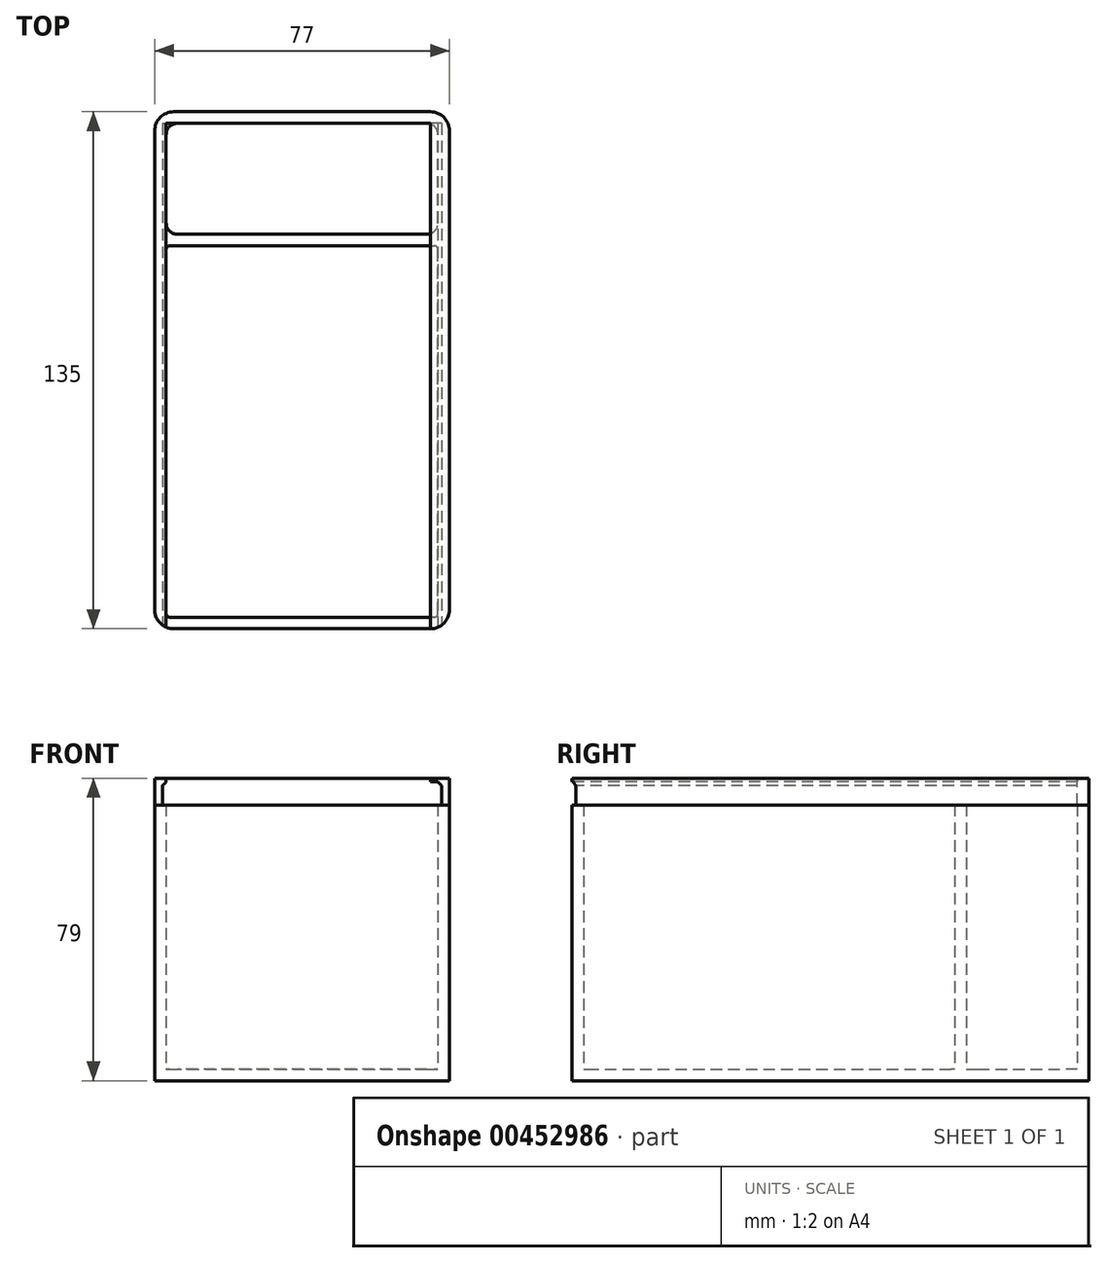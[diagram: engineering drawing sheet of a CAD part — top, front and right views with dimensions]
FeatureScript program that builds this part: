
annotation { "Feature Type Name" : "Feature", "Feature Type Description" : "" }
export const myFeature = defineFeature(function(context is Context, id is Id, definition is map)
    precondition{}
    {
        {
            var Q0;
            Q0=qCreatedBy(makeId("Top.planeOp"),FACE);
            var sketch = newSketch(context, id + "F0", { "sketchPlane" : qUnion([Q0])});
            skLineSegment(sketch, "E0.bottom", {"start": v(42.74, -68.6) * mm, "end": v(-26.26, -68.6) * mm});
            skLineSegment(sketch, "E0.top", {"start": v(43.74, 31.4) * mm, "end": v(-27.26, 31.4) * mm});
            skLineSegment(sketch, "E0.left", {"start": v(43.74, -67.6) * mm, "end": v(43.74, 27.4) * mm});
            skLineSegment(sketch, "E0.right", {"start": v(-27.26, -67.6) * mm, "end": v(-27.26, 27.4) * mm});
            skLineSegment(sketch, "E1.bottom", {"start": v(-27.26, 31.4) * mm, "end": v(43.74, 31.4) * mm});
            skLineSegment(sketch, "E1.top", {"start": v(-24.26, 60.4) * mm, "end": v(40.74, 60.4) * mm});
            skLineSegment(sketch, "E1.left", {"start": v(-27.26, 34.4) * mm, "end": v(-27.26, 57.4) * mm});
            skLineSegment(sketch, "E1.right", {"start": v(43.74, 34.4) * mm, "end": v(43.74, 57.4) * mm});
            skLineSegment(sketch, "E2.bottom", {"start": v(-26.26, 31.4) * mm, "end": v(42.74, 31.4) * mm});
            skLineSegment(sketch, "E2.top", {"start": v(-26.26, 28.4) * mm, "end": v(42.74, 28.4) * mm});
            skLineSegment(sketch, "E2.left", {"start": v(-27.26, 30.4) * mm, "end": v(-27.26, 29.4) * mm});
            skLineSegment(sketch, "E2.right", {"start": v(43.74, 30.4) * mm, "end": v(43.74, 29.4) * mm});
            skLineSegment(sketch, "E3.bottom", {"start": v(-25.26, 63.4) * mm, "end": v(41.74, 63.4) * mm});
            skLineSegment(sketch, "E3.top", {"start": v(-25.26, -71.6) * mm, "end": v(41.74, -71.6) * mm});
            skLineSegment(sketch, "E3.left", {"start": v(-30.26, 58.4) * mm, "end": v(-30.26, -66.6) * mm});
            skLineSegment(sketch, "E3.right", {"start": v(46.74, 58.4) * mm, "end": v(46.74, -66.6) * mm});
            skPoint(sketch, "E4.visualSharp", {"position": v(-30.26, 63.4) * mm});
            skArc(sketch, "E4.filletArc", {"start": v(-25.26, 63.4) * mm, "mid": v(-28.8, 61.94) * mm, "end": v(-30.26, 58.4) * mm});
            skPoint(sketch, "E5.visualSharp", {"position": v(46.74, 63.4) * mm});
            skArc(sketch, "E5.filletArc", {"start": v(46.74, 58.4) * mm, "mid": v(45.28, 61.94) * mm, "end": v(41.74, 63.4) * mm});
            skPoint(sketch, "E6.visualSharp", {"position": v(46.74, -71.6) * mm});
            skArc(sketch, "E6.filletArc", {"start": v(41.74, -71.6) * mm, "mid": v(45.28, -70.13) * mm, "end": v(46.74, -66.6) * mm});
            skPoint(sketch, "E7.visualSharp", {"position": v(-30.26, -71.6) * mm});
            skArc(sketch, "E7.filletArc", {"start": v(-30.26, -66.6) * mm, "mid": v(-28.8, -70.13) * mm, "end": v(-25.26, -71.6) * mm});
            skPoint(sketch, "E8.visualSharp", {"position": v(-27.26, -68.6) * mm});
            skArc(sketch, "E8.filletArc", {"start": v(-27.26, -67.6) * mm, "mid": v(-26.97, -68.3) * mm, "end": v(-26.26, -68.6) * mm});
            skPoint(sketch, "E9.visualSharp", {"position": v(43.74, -68.6) * mm});
            skArc(sketch, "E9.filletArc", {"start": v(42.74, -68.6) * mm, "mid": v(43.45, -68.3) * mm, "end": v(43.74, -67.6) * mm});
            skArc(sketch, "E10.filletArc", {"start": v(-26.26, 28.4) * mm, "mid": v(-26.97, 28.11) * mm, "end": v(-27.26, 27.4) * mm});
            skArc(sketch, "E11.filletArc", {"start": v(-27.26, 29.4) * mm, "mid": v(-26.97, 28.7) * mm, "end": v(-26.26, 28.4) * mm});
            skArc(sketch, "E12.filletArc", {"start": v(43.74, 27.4) * mm, "mid": v(43.45, 28.11) * mm, "end": v(42.74, 28.4) * mm});
            skArc(sketch, "E13.filletArc", {"start": v(42.74, 28.4) * mm, "mid": v(43.45, 28.7) * mm, "end": v(43.74, 29.4) * mm});
            skPoint(sketch, "E14.visualSharp", {"position": v(-27.26, 31.4) * mm});
            skArc(sketch, "E14.filletArc", {"start": v(-27.26, 34.4) * mm, "mid": v(-26.38, 32.28) * mm, "end": v(-24.26, 31.4) * mm});
            skArc(sketch, "E15.filletArc", {"start": v(-26.26, 31.4) * mm, "mid": v(-26.97, 31.11) * mm, "end": v(-27.26, 30.4) * mm});
            skPoint(sketch, "E16.visualSharp", {"position": v(43.74, 31.4) * mm});
            skArc(sketch, "E16.filletArc", {"start": v(40.74, 31.4) * mm, "mid": v(42.86, 32.28) * mm, "end": v(43.74, 34.4) * mm});
            skArc(sketch, "E17.filletArc", {"start": v(43.74, 30.4) * mm, "mid": v(43.45, 31.11) * mm, "end": v(42.74, 31.4) * mm});
            skPoint(sketch, "E18.visualSharp", {"position": v(-27.26, 60.4) * mm});
            skArc(sketch, "E18.filletArc", {"start": v(-24.26, 60.4) * mm, "mid": v(-26.38, 59.52) * mm, "end": v(-27.26, 57.4) * mm});
            skPoint(sketch, "E19.visualSharp", {"position": v(43.74, 60.4) * mm});
            skArc(sketch, "E19.filletArc", {"start": v(43.74, 57.4) * mm, "mid": v(42.86, 59.52) * mm, "end": v(40.74, 60.4) * mm});
            skSolve(sketch);
        }
        {
            var Q0;
            Q0=makeQuery(id+"F0.imprint","IMPRINT",FACE,{"disambiguationData":[TD([[makeQuery(id+"F0.imprint","IMPRINT",EDGE,{"derivedFrom":sQuery(id+"F0.wireOp",EDGE,"E0.bottom")}),1.0]])]});
            var Q1;
            Q1=makeQuery(id+"F0.imprint","IMPRINT",FACE,{"disambiguationData":[TD([[makeQuery(id+"F0.imprint","IMPRINT",EDGE,{"derivedFrom":sQuery(id+"F0.wireOp",EDGE,"E2.top")}),1.0]])]});
            extrude(context, id + "F1", {"entities" : qUnion([Q0, Q1]), "depth" : 72 * mm});
        }
        {
            var Q0;
            Q0=makeQuery(id+"F0.imprint","IMPRINT",FACE,{"disambiguationData":[TD([[makeQuery(id+"F0.imprint","IMPRINT",EDGE,{"derivedFrom":sQuery(id+"F0.wireOp",EDGE,"E1.top")}),-1.0]])]});
            var Q1;
            Q1=makeQuery(id+"F0.imprint","IMPRINT",FACE,{"disambiguationData":[TD([[makeQuery(id+"F0.imprint","IMPRINT",EDGE,{"derivedFrom":sQuery(id+"F0.wireOp",EDGE,"E0.bottom")}),-1.0]])]});
            extrude(context, id + "F2", {"entities" : qUnion([Q0, Q1]), "operationType" : NewBodyOperationType.ADD, "depth" : 3 * mm});
        }
        {
            var Q0;
            Q0=makeQuery(id+"F1.opExtrude","CAP_FACE",FACE,{"disambiguationData":[OSD([sQuery(id+"F0.wireOp",EDGE,"E0.bottom"),sQuery(id+"F0.wireOp",EDGE,"E0.left"),sQuery(id+"F0.wireOp",EDGE,"E0.right"),sQuery(id+"F0.wireOp",EDGE,"E1.top"),sQuery(id+"F0.wireOp",EDGE,"E1.left"),sQuery(id+"F0.wireOp",EDGE,"E1.right"),sQuery(id+"F0.wireOp",EDGE,"E2.bottom"),sQuery(id+"F0.wireOp",EDGE,"E2.top"),sQuery(id+"F0.wireOp",EDGE,"E3.bottom"),sQuery(id+"F0.wireOp",EDGE,"E3.top"),sQuery(id+"F0.wireOp",EDGE,"E3.left"),sQuery(id+"F0.wireOp",EDGE,"E3.right"),sQuery(id+"F0.wireOp",EDGE,"E4.filletArc"),sQuery(id+"F0.wireOp",EDGE,"E5.filletArc"),sQuery(id+"F0.wireOp",EDGE,"E6.filletArc"),sQuery(id+"F0.wireOp",EDGE,"E7.filletArc"),sQuery(id+"F0.wireOp",EDGE,"E8.filletArc"),sQuery(id+"F0.wireOp",EDGE,"E9.filletArc"),sQuery(id+"F0.wireOp",EDGE,"E10.filletArc"),sQuery(id+"F0.wireOp",EDGE,"E12.filletArc"),sQuery(id+"F0.wireOp",EDGE,"E14.filletArc"),sQuery(id+"F0.wireOp",EDGE,"E16.filletArc"),sQuery(id+"F0.wireOp",EDGE,"E18.filletArc"),sQuery(id+"F0.wireOp",EDGE,"E19.filletArc")])],"isStart":false});
            cPlane(context, id + "F3", {"entities" : qUnion([Q0]), "cplaneType" : CPlaneType.OFFSET, "offset" : 0 * mm, "width" : 150 * mm, "height" : 150 * mm});
        }
        {
            var Q0;
            Q0=qCreatedBy(id+"F3.planeOp",FACE);
            var sketch = newSketch(context, id + "F4", { "sketchPlane" : qUnion([Q0])});
            skLineSegment(sketch, "E20.bottom", {"start": v(-25.26, 63.4) * mm, "end": v(41.74, 63.4) * mm});
            skLineSegment(sketch, "E20.top", {"start": v(-25.26, -71.6) * mm, "end": v(41.74, -71.6) * mm});
            skLineSegment(sketch, "E20.left", {"start": v(-30.26, 58.4) * mm, "end": v(-30.26, -66.6) * mm});
            skLineSegment(sketch, "E20.right", {"start": v(46.74, 58.4) * mm, "end": v(46.74, -66.6) * mm});
            skArc(sketch, "E21.filletArc", {"start": v(-25.26, 63.4) * mm, "mid": v(-28.8, 61.94) * mm, "end": v(-30.26, 58.4) * mm});
            skArc(sketch, "E22.filletArc", {"start": v(46.74, 58.4) * mm, "mid": v(45.28, 61.94) * mm, "end": v(41.74, 63.4) * mm});
            skArc(sketch, "E23.filletArc", {"start": v(41.74, -71.6) * mm, "mid": v(45.28, -70.13) * mm, "end": v(46.74, -66.6) * mm});
            skArc(sketch, "E24.filletArc", {"start": v(-30.26, -66.6) * mm, "mid": v(-28.8, -70.13) * mm, "end": v(-25.26, -71.6) * mm});
            skPoint(sketch, "E25.visualSharp", {"position": v(-27.26, 45.69) * mm});
            skSolve(sketch);
        }
        {
            var Q0;
            Q0=makeQuery(id+"F4.imprint","IMPRINT",FACE,{"disambiguationData":[TD([[makeQuery(id+"F4.imprint","IMPRINT",EDGE,{"derivedFrom":sQuery(id+"F4.wireOp",EDGE,"E20.top")}),1.0]])]});
            extrude(context, id + "F5", {"entities" : qUnion([Q0]), "depth" : 7 * mm});
        }
        {
            var Q0;
            Q0=makeQuery(id+"F5.opExtrude","SWEPT_FACE",FACE,{"disambiguationData":[OSD([sQuery(id+"F4.wireOp",EDGE,"E20.top")])]});
            var sketch = newSketch(context, id + "F6", { "sketchPlane" : qUnion([Q0])});
            skLineSegment(sketch, "E26", {"start": v(41.74, 72) * mm, "end": v(44.74, 72) * mm});
            skLineSegment(sketch, "E27", {"start": v(44.74, 72) * mm, "end": v(44.74, 78) * mm});
            skLineSegment(sketch, "E28", {"start": v(44.74, 78) * mm, "end": v(41.74, 78) * mm});
            skLineSegment(sketch, "E29", {"start": v(41.74, 78) * mm, "end": v(41.74, 72) * mm});
            skLineSegment(sketch, "E30.bottom", {"start": v(-25.26, 72) * mm, "end": v(-28.26, 72) * mm});
            skLineSegment(sketch, "E30.top", {"start": v(-25.26, 78) * mm, "end": v(-28.26, 78) * mm});
            skLineSegment(sketch, "E30.left", {"start": v(-25.26, 72) * mm, "end": v(-25.26, 78) * mm});
            skLineSegment(sketch, "E30.right", {"start": v(-28.26, 72) * mm, "end": v(-28.26, 78) * mm});
            skLineSegment(sketch, "E31.top", {"start": v(-25.26, 81) * mm, "end": v(-27.26, 81) * mm});
            skLineSegment(sketch, "E31.left", {"start": v(-25.26, 78) * mm, "end": v(-25.26, 81) * mm});
            skLineSegment(sketch, "E31.right", {"start": v(-27.26, 78) * mm, "end": v(-27.26, 81) * mm});
            skLineSegment(sketch, "E32.left", {"start": v(41.74, 78) * mm, "end": v(41.74, 78) * mm});
            skLineSegment(sketch, "E32.right", {"start": v(44.74, 78) * mm, "end": v(44.74, 78) * mm});
            skLineSegment(sketch, "E33.bottom", {"start": v(43.74, 78) * mm, "end": v(41.74, 78) * mm});
            skLineSegment(sketch, "E33.top", {"start": v(43.74, 81) * mm, "end": v(41.74, 81) * mm});
            skLineSegment(sketch, "E33.left", {"start": v(43.74, 78) * mm, "end": v(43.74, 81) * mm});
            skLineSegment(sketch, "E33.right", {"start": v(41.74, 78) * mm, "end": v(41.74, 81) * mm});
            skLineSegment(sketch, "E34", {"start": v(-28.26, 78) * mm, "end": v(-28.26, 77) * mm});
            skLineSegment(sketch, "E35", {"start": v(-28.26, 77) * mm, "end": v(-27.26, 78) * mm});
            skLineSegment(sketch, "E36", {"start": v(44.74, 78) * mm, "end": v(44.74, 77) * mm});
            skLineSegment(sketch, "E37", {"start": v(44.74, 77) * mm, "end": v(43.74, 78) * mm});
            skSolve(sketch);
        }
        {
            var Q0;
            {var subQ2=sQuery(id+"F6.wireOp",EDGE,"E31.top");Q0=makeQuery(id+"F6.imprint","IMPRINT",FACE,{"disambiguationData":[TD([[makeQuery(id+"F6.imprint","IMPRINT",EDGE,{"derivedFrom":subQ2}),1.0]])]});}
            var Q1;
            Q1=makeQuery(id+"F6.imprint","IMPRINT",FACE,{"disambiguationData":[TD([[makeQuery(id+"F6.imprint","IMPRINT",EDGE,{"derivedFrom":sQuery(id+"F6.wireOp",EDGE,"E30.bottom")}),-1.0]])]});
            var Q2;
            {var subQ5=sQuery(id+"F6.wireOp",EDGE,"E29");Q2=makeQuery(id+"F6.imprint","IMPRINT",FACE,{"disambiguationData":[TD([[makeQuery(id+"F6.imprint","IMPRINT",EDGE,{"derivedFrom":subQ5}),-1.0]])]});}
            var Q3;
            {var subQ3=sQuery(id+"F6.wireOp",EDGE,"E33.bottom");Q3=makeQuery(id+"F6.imprint","IMPRINT",FACE,{"disambiguationData":[TD([[makeQuery(id+"F6.imprint","IMPRINT",EDGE,{"derivedFrom":subQ3}),-1.0]])]});}
            var Q4;
            Q4=makeQuery(id+"F6.imprint","IMPRINT",FACE,{"disambiguationData":[TD([[makeQuery(id+"F6.imprint","IMPRINT",EDGE,{"derivedFrom":sQuery(id+"F6.wireOp",EDGE,"E26")}),1.0]])]});
            var Q5;
            Q5=makeQuery(id+"F1.opExtrude","SWEPT_FACE",FACE,{"disambiguationData":[OSD([sQuery(id+"F0.wireOp",EDGE,"E1.top")])]});
            extrude(context, id + "F7", {"entities" : qUnion([Q0, Q1, Q2, Q3, Q4]), "operationType" : NewBodyOperationType.REMOVE, "endBound" : BoundingType.UP_TO_SURFACE, "oppositeDirection" : true, "endBoundEntityFace" : qUnion([Q5]), "depth" : 25 * mm});
        }
    });
